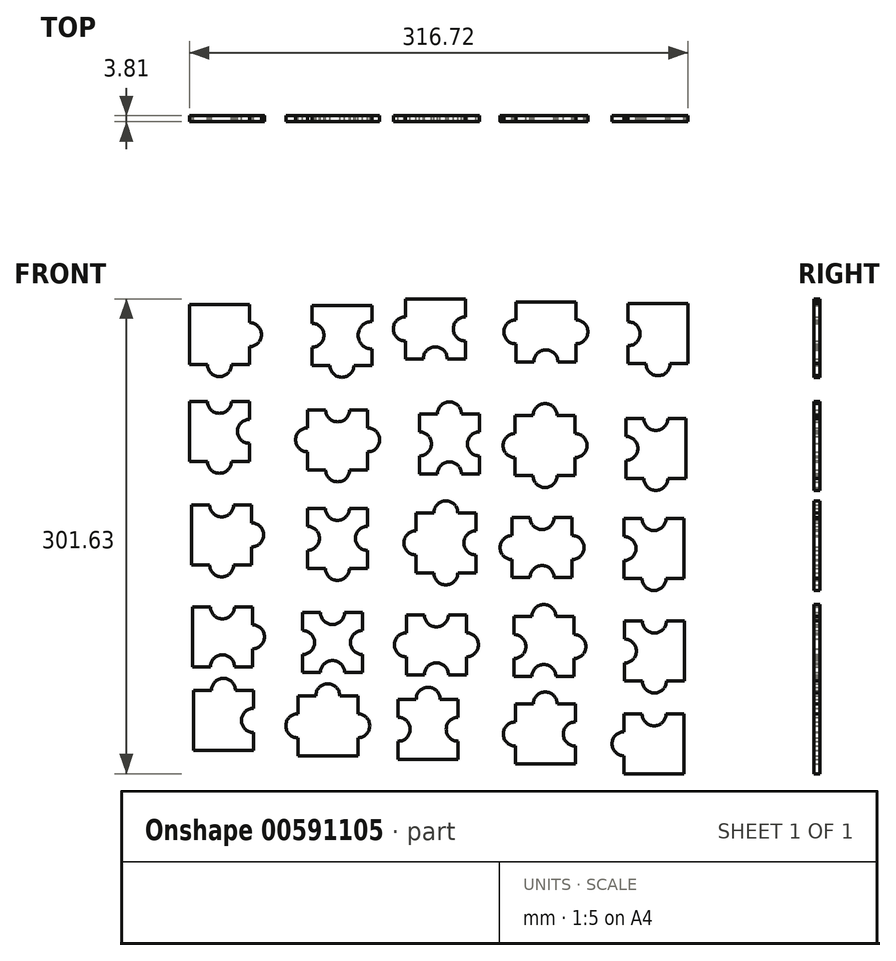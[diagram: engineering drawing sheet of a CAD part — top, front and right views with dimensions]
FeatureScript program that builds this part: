
annotation { "Feature Type Name" : "Feature", "Feature Type Description" : "" }
export const myFeature = defineFeature(function(context is Context, id is Id, definition is map)
    precondition{}
    {
        {
            var Q0;
            Q0=qCreatedBy(makeId("Front.planeOp"),FACE);
            var sketch = newSketch(context, id + "F0", { "sketchPlane" : qUnion([Q0])});
            skLineSegment(sketch, "E0", {"start": v(-60.62, 34.47) * mm, "end": v(-60.62, -3.63) * mm});
            skLineSegment(sketch, "E1", {"start": v(-60.62, 34.47) * mm, "end": v(-22.52, 34.47) * mm});
            skLineSegment(sketch, "E2", {"start": v(-22.52, 34.47) * mm, "end": v(-22.52, -3.63) * mm});
            skLineSegment(sketch, "E3", {"start": v(-22.52, -3.63) * mm, "end": v(-60.62, -3.63) * mm});
            skArc(sketch, "E4", {"start": v(-22.52, 23.04) * mm, "mid": v(-14.9, 15.42) * mm, "end": v(-22.52, 7.8) * mm});
            skArc(sketch, "E5", {"start": v(-33.95, -3.63) * mm, "mid": v(-41.57, -11.25) * mm, "end": v(-49.19, -3.63) * mm});
            skSolve(sketch);
        }
        {
            var Q0;
            Q0 = qSketchRegion(id + "F0", true);
            extrude(context, id + "F1", {"entities" : qUnion([Q0]), "depth" : 3.8 * mm, "offsetDistance" : 25.4 * mm});
        }
        {
            var Q0;
            Q0=qCreatedBy(makeId("Front.planeOp"),FACE);
            var sketch = newSketch(context, id + "F2", { "sketchPlane" : qUnion([Q0])});
            skLineSegment(sketch, "E6", {"start": v(-60.56, -26.98) * mm, "end": v(-60.56, -65.08) * mm});
            skLineSegment(sketch, "E7", {"start": v(-60.56, -26.98) * mm, "end": v(-49.13, -26.98) * mm});
            skLineSegment(sketch, "E8", {"start": v(-22.46, -26.98) * mm, "end": v(-22.46, -38.4) * mm});
            skLineSegment(sketch, "E9", {"start": v(-22.46, -65.08) * mm, "end": v(-33.89, -65.08) * mm});
            skArc(sketch, "E10", {"start": v(-33.89, -26.98) * mm, "mid": v(-41.5, -34.6) * mm, "end": v(-49.13, -26.98) * mm});
            skLineSegment(sketch, "E11.trimOffspring", {"start": v(-33.89, -26.98) * mm, "end": v(-22.46, -26.98) * mm});
            skArc(sketch, "E12", {"start": v(-22.46, -38.4) * mm, "mid": v(-30.08, -46.03) * mm, "end": v(-22.46, -53.65) * mm});
            skLineSegment(sketch, "E13.trimOffspring", {"start": v(-22.46, -53.65) * mm, "end": v(-22.46, -65.08) * mm});
            skArc(sketch, "E14", {"start": v(-33.89, -65.08) * mm, "mid": v(-41.5, -72.7) * mm, "end": v(-49.13, -65.08) * mm});
            skLineSegment(sketch, "E15.trimOffspring", {"start": v(-49.13, -65.08) * mm, "end": v(-60.56, -65.08) * mm});
            skSolve(sketch);
        }
        {
            var Q0;
            Q0 = qSketchRegion(id + "F2", true);
            extrude(context, id + "F3", {"entities" : qUnion([Q0]), "depth" : 3.8 * mm, "offsetDistance" : 25.4 * mm});
        }
        {
            var Q0;
            Q0=qCreatedBy(makeId("Front.planeOp"),FACE);
            var sketch = newSketch(context, id + "F4", { "sketchPlane" : qUnion([Q0])});
            skLineSegment(sketch, "E16", {"start": v(17.21, 34.03) * mm, "end": v(55.31, 34.03) * mm});
            skLineSegment(sketch, "E17", {"start": v(55.31, 34.03) * mm, "end": v(55.31, 23.73) * mm});
            skLineSegment(sketch, "E18", {"start": v(55.31, -4.07) * mm, "end": v(43.88, -4.07) * mm});
            skLineSegment(sketch, "E19", {"start": v(17.21, -4.07) * mm, "end": v(17.21, 7.36) * mm});
            skArc(sketch, "E20", {"start": v(17.21, 22.6) * mm, "mid": v(24.83, 14.98) * mm, "end": v(17.21, 7.36) * mm});
            skArc(sketch, "E21", {"start": v(43.88, -4.07) * mm, "mid": v(36.26, -11.7) * mm, "end": v(28.64, -4.07) * mm});
            skArc(sketch, "E22", {"start": v(55.31, 23.73) * mm, "mid": v(46.56, 14.98) * mm, "end": v(55.31, 6.23) * mm});
            skLineSegment(sketch, "E23.trimOffspring", {"start": v(55.31, 6.23) * mm, "end": v(55.31, -4.07) * mm});
            skLineSegment(sketch, "E24.trimOffspring", {"start": v(17.21, 22.6) * mm, "end": v(17.21, 34.03) * mm});
            skLineSegment(sketch, "E25.trimOffspring", {"start": v(28.64, -4.07) * mm, "end": v(17.21, -4.07) * mm});
            skSolve(sketch);
        }
        {
            var Q0;
            Q0=makeQuery(id+"F4.imprint","IMPRINT",FACE,{"disambiguationData":[TD([[makeQuery(id+"F4.imprint","IMPRINT",EDGE,{"derivedFrom":sQuery(id+"F4.wireOp",EDGE,"E16")}),-1.0]])]});
            extrude(context, id + "F5", {"entities" : qUnion([Q0]), "depth" : 3.8 * mm, "offsetDistance" : 25.4 * mm});
        }
        {
            var Q0;
            Q0=qCreatedBy(makeId("Front.planeOp"),FACE);
            var sketch = newSketch(context, id + "F6", { "sketchPlane" : qUnion([Q0])});
            skLineSegment(sketch, "E26", {"start": v(14.5, -32.37) * mm, "end": v(25.93, -32.37) * mm});
            skLineSegment(sketch, "E27", {"start": v(52.6, -32.37) * mm, "end": v(52.6, -43.8) * mm});
            skLineSegment(sketch, "E28", {"start": v(52.6, -70.47) * mm, "end": v(41.17, -70.47) * mm});
            skLineSegment(sketch, "E29", {"start": v(14.5, -70.47) * mm, "end": v(14.5, -59.04) * mm});
            skArc(sketch, "E30", {"start": v(41.17, -32.37) * mm, "mid": v(33.55, -40) * mm, "end": v(25.93, -32.37) * mm});
            skArc(sketch, "E31", {"start": v(14.5, -43.8) * mm, "mid": v(6.88, -51.42) * mm, "end": v(14.5, -59.04) * mm});
            skArc(sketch, "E32", {"start": v(52.6, -43.8) * mm, "mid": v(60.22, -51.42) * mm, "end": v(52.6, -59.04) * mm});
            skArc(sketch, "E33", {"start": v(41.17, -70.47) * mm, "mid": v(33.55, -78.1) * mm, "end": v(25.93, -70.47) * mm});
            skLineSegment(sketch, "E34.trimOffspring", {"start": v(41.17, -32.37) * mm, "end": v(52.6, -32.37) * mm});
            skLineSegment(sketch, "E35.trimOffspring", {"start": v(14.5, -43.8) * mm, "end": v(14.5, -32.37) * mm});
            skLineSegment(sketch, "E36.trimOffspring", {"start": v(52.6, -59.04) * mm, "end": v(52.6, -70.47) * mm});
            skLineSegment(sketch, "E37.trimOffspring", {"start": v(25.93, -70.47) * mm, "end": v(14.5, -70.47) * mm});
            skSolve(sketch);
        }
        {
            var Q0;
            Q0=makeQuery(id+"F6.imprint","IMPRINT",FACE,{"disambiguationData":[TD([[makeQuery(id+"F6.imprint","IMPRINT",EDGE,{"derivedFrom":sQuery(id+"F6.wireOp",EDGE,"E26")}),-1.0]])]});
            extrude(context, id + "F7", {"entities" : qUnion([Q0]), "depth" : 3.8 * mm, "offsetDistance" : 25.4 * mm});
        }
        {
            var Q0;
            Q0=qCreatedBy(makeId("Front.planeOp"),FACE);
            var sketch = newSketch(context, id + "F8", { "sketchPlane" : qUnion([Q0])});
            skLineSegment(sketch, "E38", {"start": v(76.49, 38.1) * mm, "end": v(114.59, 38.1) * mm});
            skLineSegment(sketch, "E39", {"start": v(114.59, 38.1) * mm, "end": v(114.59, 26.67) * mm});
            skLineSegment(sketch, "E40", {"start": v(114.59, 0) * mm, "end": v(103.16, 0) * mm});
            skLineSegment(sketch, "E41", {"start": v(76.49, 0) * mm, "end": v(76.49, 11.43) * mm});
            skArc(sketch, "E42", {"start": v(76.49, 26.67) * mm, "mid": v(68.87, 19.05) * mm, "end": v(76.49, 11.43) * mm});
            skArc(sketch, "E43", {"start": v(114.59, 26.67) * mm, "mid": v(106.97, 19.05) * mm, "end": v(114.59, 11.43) * mm});
            skArc(sketch, "E44", {"start": v(103.16, 0) * mm, "mid": v(95.54, 7.62) * mm, "end": v(87.92, 0) * mm});
            skLineSegment(sketch, "E45.trimOffspring", {"start": v(76.49, 26.67) * mm, "end": v(76.49, 38.1) * mm});
            skLineSegment(sketch, "E46.trimOffspring", {"start": v(114.59, 11.43) * mm, "end": v(114.59, 0) * mm});
            skLineSegment(sketch, "E47.trimOffspring", {"start": v(87.92, 0) * mm, "end": v(76.49, 0) * mm});
            skSolve(sketch);
        }
        {
            var Q0;
            Q0=makeQuery(id+"F8.imprint","IMPRINT",FACE,{"disambiguationData":[TD([[makeQuery(id+"F8.imprint","IMPRINT",EDGE,{"derivedFrom":sQuery(id+"F8.wireOp",EDGE,"E38")}),-1.0]])]});
            extrude(context, id + "F9", {"entities" : qUnion([Q0]), "depth" : 3.8 * mm, "offsetDistance" : 25.4 * mm});
        }
        {
            var Q0;
            Q0=qCreatedBy(makeId("Front.planeOp"),FACE);
            var sketch = newSketch(context, id + "F10", { "sketchPlane" : qUnion([Q0])});
            skLineSegment(sketch, "E48", {"start": v(123.53, -34.98) * mm, "end": v(123.53, -46.41) * mm});
            skLineSegment(sketch, "E49", {"start": v(123.53, -73.08) * mm, "end": v(112.1, -73.08) * mm});
            skLineSegment(sketch, "E50", {"start": v(85.43, -73.08) * mm, "end": v(85.43, -61.65) * mm});
            skArc(sketch, "E51", {"start": v(112.1, -34.98) * mm, "mid": v(104.48, -27.36) * mm, "end": v(96.86, -34.98) * mm});
            skArc(sketch, "E52", {"start": v(85.43, -46.41) * mm, "mid": v(93.05, -54.03) * mm, "end": v(85.43, -61.65) * mm});
            skArc(sketch, "E53", {"start": v(112.1, -73.08) * mm, "mid": v(104.48, -65.46) * mm, "end": v(96.86, -73.08) * mm});
            skArc(sketch, "E54", {"start": v(123.53, -46.41) * mm, "mid": v(115.91, -54.03) * mm, "end": v(123.53, -61.65) * mm});
            skLineSegment(sketch, "E55.trimOffspring", {"start": v(112.1, -34.98) * mm, "end": v(123.53, -34.98) * mm});
            skLineSegment(sketch, "E56.trimOffspring", {"start": v(123.53, -61.65) * mm, "end": v(123.53, -73.08) * mm});
            skLineSegment(sketch, "E57.trimOffspring", {"start": v(96.86, -73.08) * mm, "end": v(85.43, -73.08) * mm});
            skLineSegment(sketch, "E58.trimOffspring", {"start": v(85.43, -46.41) * mm, "end": v(85.43, -34.98) * mm});
            skLineSegment(sketch, "E59", {"start": v(85.43, -34.98) * mm, "end": v(96.86, -34.98) * mm});
            skSolve(sketch);
        }
        {
            var Q0;
            Q0=makeQuery(id+"F10.imprint","IMPRINT",FACE,{"disambiguationData":[TD([[makeQuery(id+"F10.imprint","IMPRINT",EDGE,{"derivedFrom":sQuery(id+"F10.wireOp",EDGE,"E48")}),-1.0]])]});
            extrude(context, id + "F11", {"entities" : qUnion([Q0]), "depth" : 3.8 * mm, "offsetDistance" : 25.4 * mm});
        }
        {
            var Q0;
            Q0=qCreatedBy(makeId("Front.planeOp"),FACE);
            var sketch = newSketch(context, id + "F12", { "sketchPlane" : qUnion([Q0])});
            skLineSegment(sketch, "E60", {"start": v(146.21, -36.05) * mm, "end": v(157.64, -36.05) * mm});
            skLineSegment(sketch, "E61", {"start": v(184.31, -74.15) * mm, "end": v(184.31, -62.72) * mm});
            skLineSegment(sketch, "E62", {"start": v(146.21, -36.05) * mm, "end": v(146.21, -47.48) * mm});
            skLineSegment(sketch, "E63", {"start": v(146.21, -74.15) * mm, "end": v(157.64, -74.15) * mm});
            skArc(sketch, "E64", {"start": v(172.88, -36.05) * mm, "mid": v(165.26, -28.43) * mm, "end": v(157.64, -36.05) * mm});
            skArc(sketch, "E65", {"start": v(146.21, -47.48) * mm, "mid": v(138.6, -55.1) * mm, "end": v(146.21, -62.72) * mm});
            skArc(sketch, "E66", {"start": v(172.88, -74.15) * mm, "mid": v(165.26, -81.77) * mm, "end": v(157.64, -74.15) * mm});
            skArc(sketch, "E67", {"start": v(184.31, -47.48) * mm, "mid": v(191.93, -55.1) * mm, "end": v(184.31, -62.72) * mm});
            skLineSegment(sketch, "E68.trimOffspring", {"start": v(172.88, -36.05) * mm, "end": v(184.31, -36.05) * mm});
            skLineSegment(sketch, "E69.trimOffspring", {"start": v(146.21, -62.72) * mm, "end": v(146.21, -74.15) * mm});
            skLineSegment(sketch, "E70.trimOffspring", {"start": v(172.88, -74.15) * mm, "end": v(184.31, -74.15) * mm});
            skLineSegment(sketch, "E71.trimOffspring", {"start": v(184.31, -47.48) * mm, "end": v(184.31, -36.05) * mm});
            skSolve(sketch);
        }
        {
            var Q0;
            Q0=makeQuery(id+"F12.imprint","IMPRINT",FACE,{"disambiguationData":[TD([[makeQuery(id+"F12.imprint","IMPRINT",EDGE,{"derivedFrom":sQuery(id+"F12.wireOp",EDGE,"E60")}),-1.0]])]});
            extrude(context, id + "F13", {"entities" : qUnion([Q0]), "depth" : 3.8 * mm, "offsetDistance" : 25.4 * mm});
        }
        {
            var Q0;
            Q0=qCreatedBy(makeId("Front.planeOp"),FACE);
            var sketch = newSketch(context, id + "F14", { "sketchPlane" : qUnion([Q0])});
            skLineSegment(sketch, "E72", {"start": v(146.72, 36.22) * mm, "end": v(184.82, 36.22) * mm});
            skLineSegment(sketch, "E73", {"start": v(184.82, 36.22) * mm, "end": v(184.82, 24.79) * mm});
            skLineSegment(sketch, "E74", {"start": v(184.82, -1.88) * mm, "end": v(173.39, -1.88) * mm});
            skLineSegment(sketch, "E75", {"start": v(146.72, -1.88) * mm, "end": v(146.72, 9.55) * mm});
            skArc(sketch, "E76", {"start": v(146.72, 24.79) * mm, "mid": v(139.1, 17.17) * mm, "end": v(146.72, 9.55) * mm});
            skArc(sketch, "E77", {"start": v(173.39, -1.88) * mm, "mid": v(165.77, 5.74) * mm, "end": v(158.15, -1.88) * mm});
            skArc(sketch, "E78", {"start": v(184.82, 9.55) * mm, "mid": v(192.44, 17.17) * mm, "end": v(184.82, 24.79) * mm});
            skLineSegment(sketch, "E79.trimOffspring", {"start": v(158.15, -1.88) * mm, "end": v(146.72, -1.88) * mm});
            skLineSegment(sketch, "E80.trimOffspring", {"start": v(184.82, 9.55) * mm, "end": v(184.82, -1.88) * mm});
            skLineSegment(sketch, "E81.trimOffspring", {"start": v(146.72, 24.79) * mm, "end": v(146.72, 36.22) * mm});
            skSolve(sketch);
        }
        {
            var Q0;
            Q0=makeQuery(id+"F14.imprint","IMPRINT",FACE,{"disambiguationData":[TD([[makeQuery(id+"F14.imprint","IMPRINT",EDGE,{"derivedFrom":sQuery(id+"F14.wireOp",EDGE,"E72")}),-1.0]])]});
            extrude(context, id + "F15", {"entities" : qUnion([Q0]), "depth" : 3.8 * mm, "offsetDistance" : 25.4 * mm});
        }
        {
            var Q0;
            Q0=qCreatedBy(makeId("Front.planeOp"),FACE);
            var sketch = newSketch(context, id + "F16", { "sketchPlane" : qUnion([Q0])});
            skLineSegment(sketch, "E82", {"start": v(218, 35) * mm, "end": v(256.1, 35) * mm});
            skLineSegment(sketch, "E83", {"start": v(256.1, 35) * mm, "end": v(256.1, -3.1) * mm});
            skLineSegment(sketch, "E84", {"start": v(256.1, -3.1) * mm, "end": v(244.67, -3.1) * mm});
            skLineSegment(sketch, "E85", {"start": v(218, -3.1) * mm, "end": v(218, 8.32) * mm});
            skArc(sketch, "E86", {"start": v(218, 8.32) * mm, "mid": v(225.62, 15.94) * mm, "end": v(218, 23.56) * mm});
            skArc(sketch, "E87", {"start": v(244.67, -3.1) * mm, "mid": v(237.05, -10.73) * mm, "end": v(229.43, -3.1) * mm});
            skLineSegment(sketch, "E88.trimOffspring", {"start": v(218, 23.56) * mm, "end": v(218, 35) * mm});
            skLineSegment(sketch, "E89.trimOffspring", {"start": v(229.43, -3.1) * mm, "end": v(218, -3.1) * mm});
            skSolve(sketch);
        }
        {
            var Q0;
            Q0=makeQuery(id+"F16.imprint","IMPRINT",FACE,{"disambiguationData":[TD([[makeQuery(id+"F16.imprint","IMPRINT",EDGE,{"derivedFrom":sQuery(id+"F16.wireOp",EDGE,"E82")}),-1.0]])]});
            extrude(context, id + "F17", {"entities" : qUnion([Q0]), "depth" : 3.8 * mm, "offsetDistance" : 25.4 * mm});
        }
        {
            var Q0;
            Q0=qCreatedBy(makeId("Front.planeOp"),FACE);
            var sketch = newSketch(context, id + "F18", { "sketchPlane" : qUnion([Q0])});
            skLineSegment(sketch, "E90", {"start": v(216.58, -37.87) * mm, "end": v(228, -37.87) * mm});
            skLineSegment(sketch, "E91", {"start": v(254.68, -37.87) * mm, "end": v(254.68, -75.97) * mm});
            skLineSegment(sketch, "E92", {"start": v(254.68, -75.97) * mm, "end": v(243.25, -75.97) * mm});
            skLineSegment(sketch, "E93", {"start": v(216.58, -75.97) * mm, "end": v(216.58, -64.54) * mm});
            skArc(sketch, "E94", {"start": v(243.25, -37.87) * mm, "mid": v(235.63, -45.49) * mm, "end": v(228, -37.87) * mm});
            skArc(sketch, "E95", {"start": v(216.58, -64.54) * mm, "mid": v(224.2, -56.92) * mm, "end": v(216.58, -49.3) * mm});
            skArc(sketch, "E96", {"start": v(243.25, -75.97) * mm, "mid": v(235.63, -83.59) * mm, "end": v(228, -75.97) * mm});
            skLineSegment(sketch, "E97.trimOffspring", {"start": v(243.25, -37.87) * mm, "end": v(254.68, -37.87) * mm});
            skLineSegment(sketch, "E98.trimOffspring", {"start": v(216.58, -49.3) * mm, "end": v(216.58, -37.87) * mm});
            skLineSegment(sketch, "E99.trimOffspring", {"start": v(228, -75.97) * mm, "end": v(216.58, -75.97) * mm});
            skSolve(sketch);
        }
        {
            var Q0;
            Q0=makeQuery(id+"F18.imprint","IMPRINT",FACE,{"disambiguationData":[TD([[makeQuery(id+"F18.imprint","IMPRINT",EDGE,{"derivedFrom":sQuery(id+"F18.wireOp",EDGE,"E90")}),-1.0]])]});
            extrude(context, id + "F19", {"entities" : qUnion([Q0]), "depth" : 3.8 * mm, "offsetDistance" : 25.4 * mm});
        }
        {
            var Q0;
            Q0=qCreatedBy(makeId("Front.planeOp"),FACE);
            var sketch = newSketch(context, id + "F20", { "sketchPlane" : qUnion([Q0])});
            skLineSegment(sketch, "E100", {"start": v(-59.22, -92.7) * mm, "end": v(-47.79, -92.7) * mm});
            skLineSegment(sketch, "E101", {"start": v(-21.12, -92.7) * mm, "end": v(-21.12, -104.14) * mm});
            skLineSegment(sketch, "E102", {"start": v(-21.12, -130.8) * mm, "end": v(-32.55, -130.8) * mm});
            skLineSegment(sketch, "E103", {"start": v(-59.22, -130.8) * mm, "end": v(-59.22, -92.7) * mm});
            skArc(sketch, "E104", {"start": v(-32.55, -92.7) * mm, "mid": v(-40.17, -100.33) * mm, "end": v(-47.79, -92.7) * mm});
            skArc(sketch, "E105", {"start": v(-21.12, -104.14) * mm, "mid": v(-13.5, -111.76) * mm, "end": v(-21.12, -119.38) * mm});
            skArc(sketch, "E106", {"start": v(-32.55, -130.8) * mm, "mid": v(-40.17, -138.43) * mm, "end": v(-47.79, -130.8) * mm});
            skLineSegment(sketch, "E107.trimOffspring", {"start": v(-32.55, -92.7) * mm, "end": v(-21.12, -92.7) * mm});
            skLineSegment(sketch, "E108.trimOffspring", {"start": v(-21.12, -119.38) * mm, "end": v(-21.12, -130.8) * mm});
            skLineSegment(sketch, "E109.trimOffspring", {"start": v(-47.79, -130.8) * mm, "end": v(-59.22, -130.8) * mm});
            skSolve(sketch);
        }
        {
            var Q0;
            Q0=makeQuery(id+"F20.imprint","IMPRINT",FACE,{"disambiguationData":[TD([[makeQuery(id+"F20.imprint","IMPRINT",EDGE,{"derivedFrom":sQuery(id+"F20.wireOp",EDGE,"E100")}),-1.0]])]});
            extrude(context, id + "F21", {"entities" : qUnion([Q0]), "depth" : 3.8 * mm, "offsetDistance" : 25.4 * mm});
        }
        {
            var Q0;
            Q0=qCreatedBy(makeId("Front.planeOp"),FACE);
            var sketch = newSketch(context, id + "F22", { "sketchPlane" : qUnion([Q0])});
            skLineSegment(sketch, "E110", {"start": v(14.35, -94.97) * mm, "end": v(25.78, -94.97) * mm});
            skLineSegment(sketch, "E111", {"start": v(52.45, -94.97) * mm, "end": v(52.45, -106.4) * mm});
            skLineSegment(sketch, "E112", {"start": v(52.45, -133.07) * mm, "end": v(41.02, -133.07) * mm});
            skLineSegment(sketch, "E113", {"start": v(14.35, -133.07) * mm, "end": v(14.35, -121.64) * mm});
            skArc(sketch, "E114", {"start": v(41.02, -94.97) * mm, "mid": v(33.4, -102.6) * mm, "end": v(25.78, -94.97) * mm});
            skArc(sketch, "E115", {"start": v(14.35, -121.64) * mm, "mid": v(21.97, -114.02) * mm, "end": v(14.35, -106.4) * mm});
            skArc(sketch, "E116", {"start": v(41.02, -133.07) * mm, "mid": v(33.4, -140.7) * mm, "end": v(25.78, -133.07) * mm});
            skArc(sketch, "E117", {"start": v(52.45, -106.4) * mm, "mid": v(44.83, -114.02) * mm, "end": v(52.45, -121.64) * mm});
            skLineSegment(sketch, "E118.trimOffspring", {"start": v(41.02, -94.97) * mm, "end": v(52.45, -94.97) * mm});
            skLineSegment(sketch, "E119.trimOffspring", {"start": v(52.45, -121.64) * mm, "end": v(52.45, -133.07) * mm});
            skLineSegment(sketch, "E120.trimOffspring", {"start": v(25.78, -133.07) * mm, "end": v(14.35, -133.07) * mm});
            skLineSegment(sketch, "E121.trimOffspring", {"start": v(14.35, -106.4) * mm, "end": v(14.35, -94.97) * mm});
            skSolve(sketch);
        }
        {
            var Q0;
            Q0=makeQuery(id+"F22.imprint","IMPRINT",FACE,{"disambiguationData":[TD([[makeQuery(id+"F22.imprint","IMPRINT",EDGE,{"derivedFrom":sQuery(id+"F22.wireOp",EDGE,"E110")}),-1.0]])]});
            extrude(context, id + "F23", {"entities" : qUnion([Q0]), "depth" : 3.8 * mm, "offsetDistance" : 25.4 * mm});
        }
        {
            var Q0;
            Q0=qCreatedBy(makeId("Front.planeOp"),FACE);
            var sketch = newSketch(context, id + "F24", { "sketchPlane" : qUnion([Q0])});
            skLineSegment(sketch, "E122", {"start": v(83.18, -97.86) * mm, "end": v(94.61, -97.86) * mm});
            skLineSegment(sketch, "E123", {"start": v(121.28, -97.86) * mm, "end": v(121.28, -109.29) * mm});
            skLineSegment(sketch, "E124", {"start": v(121.28, -135.96) * mm, "end": v(109.85, -135.96) * mm});
            skLineSegment(sketch, "E125", {"start": v(83.18, -135.96) * mm, "end": v(83.18, -124.53) * mm});
            skArc(sketch, "E126", {"start": v(109.85, -97.86) * mm, "mid": v(102.23, -90.24) * mm, "end": v(94.61, -97.86) * mm});
            skArc(sketch, "E127", {"start": v(83.18, -109.29) * mm, "mid": v(75.56, -116.9) * mm, "end": v(83.18, -124.53) * mm});
            skArc(sketch, "E128", {"start": v(109.85, -135.96) * mm, "mid": v(102.23, -143.58) * mm, "end": v(94.61, -135.96) * mm});
            skArc(sketch, "E129", {"start": v(121.28, -109.29) * mm, "mid": v(113.66, -116.9) * mm, "end": v(121.28, -124.53) * mm});
            skLineSegment(sketch, "E130.trimOffspring", {"start": v(121.28, -124.53) * mm, "end": v(121.28, -135.96) * mm});
            skLineSegment(sketch, "E131.trimOffspring", {"start": v(109.85, -97.86) * mm, "end": v(121.28, -97.86) * mm});
            skLineSegment(sketch, "E132.trimOffspring", {"start": v(83.18, -109.29) * mm, "end": v(83.18, -97.86) * mm});
            skLineSegment(sketch, "E133.trimOffspring", {"start": v(94.61, -135.96) * mm, "end": v(83.18, -135.96) * mm});
            skSolve(sketch);
        }
        {
            var Q0;
            Q0=makeQuery(id+"F24.imprint","IMPRINT",FACE,{"disambiguationData":[TD([[makeQuery(id+"F24.imprint","IMPRINT",EDGE,{"derivedFrom":sQuery(id+"F24.wireOp",EDGE,"E122")}),-1.0]])]});
            extrude(context, id + "F25", {"entities" : qUnion([Q0]), "depth" : 3.8 * mm, "offsetDistance" : 25.4 * mm});
        }
        {
            var Q0;
            Q0=qCreatedBy(makeId("Front.planeOp"),FACE);
            var sketch = newSketch(context, id + "F26", { "sketchPlane" : qUnion([Q0])});
            skLineSegment(sketch, "E134", {"start": v(182.47, -100.82) * mm, "end": v(182.47, -112.25) * mm});
            skLineSegment(sketch, "E135", {"start": v(182.47, -138.92) * mm, "end": v(171.04, -138.92) * mm});
            skLineSegment(sketch, "E136", {"start": v(144.37, -138.92) * mm, "end": v(144.37, -127.5) * mm});
            skArc(sketch, "E137", {"start": v(171.04, -100.82) * mm, "mid": v(163.42, -108.44) * mm, "end": v(155.8, -100.82) * mm});
            skArc(sketch, "E138", {"start": v(144.37, -112.25) * mm, "mid": v(136.75, -119.87) * mm, "end": v(144.37, -127.5) * mm});
            skArc(sketch, "E139", {"start": v(171.04, -138.92) * mm, "mid": v(163.42, -131.3) * mm, "end": v(155.8, -138.92) * mm});
            skArc(sketch, "E140", {"start": v(182.47, -127.5) * mm, "mid": v(190.09, -119.87) * mm, "end": v(182.47, -112.25) * mm});
            skPoint(sketch, "E140.startSnap0", {"position": v(182.47, -119.87) * mm});
            skLineSegment(sketch, "E141.trimOffspring", {"start": v(171.04, -100.82) * mm, "end": v(182.47, -100.82) * mm});
            skLineSegment(sketch, "E142.trimOffspring", {"start": v(182.47, -127.5) * mm, "end": v(182.47, -138.92) * mm});
            skLineSegment(sketch, "E143.trimOffspring", {"start": v(155.8, -138.92) * mm, "end": v(144.37, -138.92) * mm});
            skLineSegment(sketch, "E144.trimOffspring", {"start": v(144.37, -112.25) * mm, "end": v(144.37, -100.82) * mm});
            skLineSegment(sketch, "E145", {"start": v(144.37, -100.82) * mm, "end": v(155.8, -100.82) * mm});
            skSolve(sketch);
        }
        {
            var Q0;
            Q0=makeQuery(id+"F26.imprint","IMPRINT",FACE,{"disambiguationData":[TD([[makeQuery(id+"F26.imprint","IMPRINT",EDGE,{"derivedFrom":sQuery(id+"F26.wireOp",EDGE,"E134")}),-1.0]])]});
            extrude(context, id + "F27", {"entities" : qUnion([Q0]), "depth" : 3.8 * mm, "offsetDistance" : 25.4 * mm});
        }
        {
            var Q0;
            Q0=qCreatedBy(makeId("Front.planeOp"),FACE);
            var sketch = newSketch(context, id + "F28", { "sketchPlane" : qUnion([Q0])});
            skLineSegment(sketch, "E146", {"start": v(215.4, -101.4) * mm, "end": v(226.83, -101.4) * mm});
            skLineSegment(sketch, "E147", {"start": v(253.5, -101.4) * mm, "end": v(253.5, -139.5) * mm});
            skLineSegment(sketch, "E148", {"start": v(253.5, -139.5) * mm, "end": v(242.07, -139.5) * mm});
            skLineSegment(sketch, "E149", {"start": v(215.4, -139.5) * mm, "end": v(215.4, -128.07) * mm});
            skArc(sketch, "E150", {"start": v(242.07, -101.4) * mm, "mid": v(234.45, -109.02) * mm, "end": v(226.83, -101.4) * mm});
            skArc(sketch, "E151", {"start": v(215.4, -112.83) * mm, "mid": v(223.02, -120.45) * mm, "end": v(215.4, -128.07) * mm});
            skArc(sketch, "E152", {"start": v(242.07, -139.5) * mm, "mid": v(234.45, -147.12) * mm, "end": v(226.83, -139.5) * mm});
            skLineSegment(sketch, "E153.trimOffspring", {"start": v(215.4, -112.83) * mm, "end": v(215.4, -101.4) * mm});
            skLineSegment(sketch, "E154.trimOffspring", {"start": v(242.07, -101.4) * mm, "end": v(253.5, -101.4) * mm});
            skLineSegment(sketch, "E155.trimOffspring", {"start": v(226.83, -139.5) * mm, "end": v(215.4, -139.5) * mm});
            skSolve(sketch);
        }
        {
            var Q0;
            Q0=makeQuery(id+"F28.imprint","IMPRINT",FACE,{"disambiguationData":[TD([[makeQuery(id+"F28.imprint","IMPRINT",EDGE,{"derivedFrom":sQuery(id+"F28.wireOp",EDGE,"E146")}),-1.0]])]});
            extrude(context, id + "F29", {"entities" : qUnion([Q0]), "depth" : 3.8 * mm, "offsetDistance" : 25.4 * mm});
        }
        {
            var Q0;
            Q0=qCreatedBy(makeId("Front.planeOp"),FACE);
            var sketch = newSketch(context, id + "F30", { "sketchPlane" : qUnion([Q0])});
            skLineSegment(sketch, "E156", {"start": v(-58.69, -157.48) * mm, "end": v(-47.26, -157.48) * mm});
            skLineSegment(sketch, "E157", {"start": v(-20.59, -157.48) * mm, "end": v(-20.59, -168.91) * mm});
            skLineSegment(sketch, "E158", {"start": v(-20.59, -195.58) * mm, "end": v(-32.02, -195.58) * mm});
            skLineSegment(sketch, "E159", {"start": v(-58.69, -195.58) * mm, "end": v(-58.69, -157.48) * mm});
            skArc(sketch, "E160", {"start": v(-32.02, -157.48) * mm, "mid": v(-39.64, -165.1) * mm, "end": v(-47.26, -157.48) * mm});
            skArc(sketch, "E161", {"start": v(-32.02, -195.58) * mm, "mid": v(-39.64, -187.96) * mm, "end": v(-47.26, -195.58) * mm});
            skArc(sketch, "E162", {"start": v(-20.59, -168.91) * mm, "mid": v(-12.97, -176.53) * mm, "end": v(-20.59, -184.15) * mm});
            skLineSegment(sketch, "E163.trimOffspring", {"start": v(-32.02, -157.48) * mm, "end": v(-20.59, -157.48) * mm});
            skLineSegment(sketch, "E164.trimOffspring", {"start": v(-20.59, -184.15) * mm, "end": v(-20.59, -195.58) * mm});
            skLineSegment(sketch, "E165.trimOffspring", {"start": v(-47.26, -195.58) * mm, "end": v(-58.69, -195.58) * mm});
            skSolve(sketch);
        }
        {
            var Q0;
            Q0=makeQuery(id+"F30.imprint","IMPRINT",FACE,{"disambiguationData":[TD([[makeQuery(id+"F30.imprint","IMPRINT",EDGE,{"derivedFrom":sQuery(id+"F30.wireOp",EDGE,"E156")}),-1.0]])]});
            extrude(context, id + "F31", {"entities" : qUnion([Q0]), "depth" : 3.8 * mm, "offsetDistance" : 25.4 * mm});
        }
        {
            var Q0;
            Q0=qCreatedBy(makeId("Front.planeOp"),FACE);
            var sketch = newSketch(context, id + "F32", { "sketchPlane" : qUnion([Q0])});
            skLineSegment(sketch, "E166", {"start": v(11.24, -161.11) * mm, "end": v(22.67, -161.11) * mm});
            skLineSegment(sketch, "E167", {"start": v(49.34, -161.11) * mm, "end": v(49.34, -172.54) * mm});
            skLineSegment(sketch, "E168", {"start": v(49.34, -199.21) * mm, "end": v(37.9, -199.21) * mm});
            skLineSegment(sketch, "E169", {"start": v(11.24, -199.21) * mm, "end": v(11.24, -187.78) * mm});
            skArc(sketch, "E170", {"start": v(37.9, -161.11) * mm, "mid": v(30.29, -168.73) * mm, "end": v(22.67, -161.11) * mm});
            skPoint(sketch, "E171.startSnap0", {"position": v(30.29, -168.73) * mm});
            skArc(sketch, "E172", {"start": v(11.24, -172.54) * mm, "mid": v(18.86, -180.16) * mm, "end": v(11.24, -187.78) * mm});
            skArc(sketch, "E173", {"start": v(37.9, -199.21) * mm, "mid": v(30.29, -191.6) * mm, "end": v(22.67, -199.21) * mm});
            skArc(sketch, "E174", {"start": v(49.34, -172.54) * mm, "mid": v(41.72, -180.16) * mm, "end": v(49.34, -187.78) * mm});
            skLineSegment(sketch, "E175.trimOffspring", {"start": v(37.9, -161.11) * mm, "end": v(49.34, -161.11) * mm});
            skLineSegment(sketch, "E176.trimOffspring", {"start": v(11.24, -172.54) * mm, "end": v(11.24, -161.11) * mm});
            skLineSegment(sketch, "E177.trimOffspring", {"start": v(22.67, -199.21) * mm, "end": v(11.24, -199.21) * mm});
            skLineSegment(sketch, "E178.trimOffspring", {"start": v(49.34, -187.78) * mm, "end": v(49.34, -199.21) * mm});
            skSolve(sketch);
        }
        {
            var Q0;
            Q0=makeQuery(id+"F32.imprint","IMPRINT",FACE,{"disambiguationData":[TD([[makeQuery(id+"F32.imprint","IMPRINT",EDGE,{"derivedFrom":sQuery(id+"F32.wireOp",EDGE,"E166")}),-1.0]])]});
            extrude(context, id + "F33", {"entities" : qUnion([Q0]), "depth" : 3.8 * mm, "offsetDistance" : 25.4 * mm});
        }
        {
            var Q0;
            Q0=qCreatedBy(makeId("Front.planeOp"),FACE);
            var sketch = newSketch(context, id + "F34", { "sketchPlane" : qUnion([Q0])});
            skLineSegment(sketch, "E179", {"start": v(77.18, -162.59) * mm, "end": v(88.61, -162.59) * mm});
            skLineSegment(sketch, "E180", {"start": v(115.28, -162.59) * mm, "end": v(115.28, -174.02) * mm});
            skLineSegment(sketch, "E181", {"start": v(115.28, -200.69) * mm, "end": v(103.85, -200.69) * mm});
            skLineSegment(sketch, "E182", {"start": v(77.18, -200.69) * mm, "end": v(77.18, -189.26) * mm});
            skArc(sketch, "E183", {"start": v(103.85, -162.59) * mm, "mid": v(96.23, -170.2) * mm, "end": v(88.61, -162.59) * mm});
            skArc(sketch, "E184", {"start": v(77.18, -174.02) * mm, "mid": v(69.56, -181.64) * mm, "end": v(77.18, -189.26) * mm});
            skArc(sketch, "E185", {"start": v(103.85, -200.69) * mm, "mid": v(96.23, -193.07) * mm, "end": v(88.61, -200.69) * mm});
            skArc(sketch, "E186", {"start": v(115.28, -174.02) * mm, "mid": v(122.9, -181.64) * mm, "end": v(115.28, -189.26) * mm});
            skLineSegment(sketch, "E187.trimOffspring", {"start": v(103.85, -162.59) * mm, "end": v(115.28, -162.59) * mm});
            skLineSegment(sketch, "E188.trimOffspring", {"start": v(115.28, -189.26) * mm, "end": v(115.28, -200.69) * mm});
            skLineSegment(sketch, "E189.trimOffspring", {"start": v(88.61, -200.69) * mm, "end": v(77.18, -200.69) * mm});
            skLineSegment(sketch, "E190.trimOffspring", {"start": v(77.18, -174.02) * mm, "end": v(77.18, -162.59) * mm});
            skSolve(sketch);
        }
        {
            var Q0;
            Q0=makeQuery(id+"F34.imprint","IMPRINT",FACE,{"disambiguationData":[TD([[makeQuery(id+"F34.imprint","IMPRINT",EDGE,{"derivedFrom":sQuery(id+"F34.wireOp",EDGE,"E179")}),-1.0]])]});
            extrude(context, id + "F35", {"entities" : qUnion([Q0]), "depth" : 3.8 * mm, "offsetDistance" : 25.4 * mm});
        }
        {
            var Q0;
            Q0=qCreatedBy(makeId("Front.planeOp"),FACE);
            var sketch = newSketch(context, id + "F36", { "sketchPlane" : qUnion([Q0])});
            skLineSegment(sketch, "E191", {"start": v(145.5, -163.65) * mm, "end": v(156.93, -163.65) * mm});
            skLineSegment(sketch, "E192", {"start": v(183.6, -163.65) * mm, "end": v(183.6, -175.08) * mm});
            skLineSegment(sketch, "E193", {"start": v(183.6, -201.75) * mm, "end": v(172.17, -201.75) * mm});
            skLineSegment(sketch, "E194", {"start": v(145.5, -201.75) * mm, "end": v(145.5, -190.32) * mm});
            skArc(sketch, "E195", {"start": v(172.17, -163.65) * mm, "mid": v(164.55, -156.03) * mm, "end": v(156.93, -163.65) * mm});
            skArc(sketch, "E196", {"start": v(145.5, -175.08) * mm, "mid": v(153.12, -182.7) * mm, "end": v(145.5, -190.32) * mm});
            skArc(sketch, "E197", {"start": v(183.6, -190.32) * mm, "mid": v(191.22, -182.7) * mm, "end": v(183.6, -175.08) * mm});
            skArc(sketch, "E198", {"start": v(172.17, -201.75) * mm, "mid": v(164.55, -194.13) * mm, "end": v(156.93, -201.75) * mm});
            skLineSegment(sketch, "E199.trimOffspring", {"start": v(172.17, -163.65) * mm, "end": v(183.6, -163.65) * mm});
            skLineSegment(sketch, "E200.trimOffspring", {"start": v(183.6, -190.32) * mm, "end": v(183.6, -201.75) * mm});
            skLineSegment(sketch, "E201.trimOffspring", {"start": v(156.93, -201.75) * mm, "end": v(145.5, -201.75) * mm});
            skLineSegment(sketch, "E202.trimOffspring", {"start": v(145.5, -175.08) * mm, "end": v(145.5, -163.65) * mm});
            skSolve(sketch);
        }
        {
            var Q0;
            Q0 = qSketchRegion(id + "F36", true);
            extrude(context, id + "F37", {"entities" : qUnion([Q0]), "depth" : 3.8 * mm, "offsetDistance" : 25.4 * mm});
        }
        {
            var Q0;
            Q0=qCreatedBy(makeId("Front.planeOp"),FACE);
            var sketch = newSketch(context, id + "F38", { "sketchPlane" : qUnion([Q0])});
            skLineSegment(sketch, "E203", {"start": v(215.68, -166.55) * mm, "end": v(227.11, -166.55) * mm});
            skLineSegment(sketch, "E204", {"start": v(253.78, -166.55) * mm, "end": v(253.78, -204.65) * mm});
            skLineSegment(sketch, "E205", {"start": v(253.78, -204.65) * mm, "end": v(242.35, -204.65) * mm});
            skLineSegment(sketch, "E206", {"start": v(215.68, -204.65) * mm, "end": v(215.68, -193.22) * mm});
            skArc(sketch, "E207", {"start": v(242.35, -166.55) * mm, "mid": v(234.73, -174.17) * mm, "end": v(227.11, -166.55) * mm});
            skArc(sketch, "E208", {"start": v(215.68, -177.98) * mm, "mid": v(223.3, -185.6) * mm, "end": v(215.68, -193.22) * mm});
            skArc(sketch, "E209", {"start": v(242.35, -204.65) * mm, "mid": v(234.73, -212.27) * mm, "end": v(227.11, -204.65) * mm});
            skLineSegment(sketch, "E210.trimOffspring", {"start": v(242.35, -166.55) * mm, "end": v(253.78, -166.55) * mm});
            skLineSegment(sketch, "E211.trimOffspring", {"start": v(215.68, -177.98) * mm, "end": v(215.68, -166.55) * mm});
            skLineSegment(sketch, "E212.trimOffspring", {"start": v(227.11, -204.65) * mm, "end": v(215.68, -204.65) * mm});
            skSolve(sketch);
        }
        {
            var Q0;
            Q0 = qSketchRegion(id + "F38", true);
            extrude(context, id + "F39", {"entities" : qUnion([Q0]), "depth" : 3.8 * mm, "offsetDistance" : 25.4 * mm});
        }
        {
            var Q0;
            Q0=qCreatedBy(makeId("Front.planeOp"),FACE);
            var sketch = newSketch(context, id + "F40", { "sketchPlane" : qUnion([Q0])});
            skLineSegment(sketch, "E213", {"start": v(-19.99, -210.62) * mm, "end": v(-19.99, -222.05) * mm});
            skLineSegment(sketch, "E214", {"start": v(-19.99, -248.72) * mm, "end": v(-58.09, -248.72) * mm});
            skLineSegment(sketch, "E215", {"start": v(-58.09, -248.72) * mm, "end": v(-58.09, -210.62) * mm});
            skArc(sketch, "E216", {"start": v(-31.42, -210.62) * mm, "mid": v(-39.04, -203) * mm, "end": v(-46.66, -210.62) * mm});
            skArc(sketch, "E217", {"start": v(-19.99, -222.05) * mm, "mid": v(-27.6, -229.67) * mm, "end": v(-19.99, -237.29) * mm});
            skLineSegment(sketch, "E218.trimOffspring", {"start": v(-31.42, -210.62) * mm, "end": v(-19.99, -210.62) * mm});
            skLineSegment(sketch, "E219.trimOffspring", {"start": v(-19.99, -237.29) * mm, "end": v(-19.99, -248.72) * mm});
            skLineSegment(sketch, "E220", {"start": v(-58.09, -210.62) * mm, "end": v(-46.66, -210.62) * mm});
            skSolve(sketch);
        }
        {
            var Q0;
            Q0 = qSketchRegion(id + "F40", true);
            extrude(context, id + "F41", {"entities" : qUnion([Q0]), "depth" : 3.8 * mm, "offsetDistance" : 25.4 * mm});
        }
        {
            var Q0;
            Q0=qCreatedBy(makeId("Front.planeOp"),FACE);
            var sketch = newSketch(context, id + "F42", { "sketchPlane" : qUnion([Q0])});
            skLineSegment(sketch, "E221", {"start": v(8.21, -214) * mm, "end": v(19.64, -214) * mm});
            skLineSegment(sketch, "E222", {"start": v(46.31, -252.1) * mm, "end": v(8.21, -252.1) * mm});
            skLineSegment(sketch, "E223", {"start": v(8.21, -252.1) * mm, "end": v(8.21, -240.66) * mm});
            skArc(sketch, "E224", {"start": v(8.21, -225.42) * mm, "mid": v(0.6, -233.04) * mm, "end": v(8.21, -240.66) * mm});
            skArc(sketch, "E225", {"start": v(34.88, -214) * mm, "mid": v(27.26, -206.37) * mm, "end": v(19.64, -214) * mm});
            skArc(sketch, "E226", {"start": v(46.31, -225.42) * mm, "mid": v(53.93, -233.04) * mm, "end": v(46.31, -240.66) * mm});
            skLineSegment(sketch, "E227.trimOffspring", {"start": v(34.88, -214) * mm, "end": v(46.31, -214) * mm});
            skLineSegment(sketch, "E228.trimOffspring", {"start": v(8.21, -225.42) * mm, "end": v(8.21, -214) * mm});
            skLineSegment(sketch, "E229.trimOffspring", {"start": v(46.31, -240.66) * mm, "end": v(46.31, -252.1) * mm});
            skLineSegment(sketch, "E230", {"start": v(46.31, -214) * mm, "end": v(46.31, -225.42) * mm});
            skSolve(sketch);
        }
        {
            var Q0;
            Q0 = qSketchRegion(id + "F42", true);
            extrude(context, id + "F43", {"entities" : qUnion([Q0]), "depth" : 3.8 * mm, "offsetDistance" : 25.4 * mm});
        }
        {
            var Q0;
            Q0=qCreatedBy(makeId("Front.planeOp"),FACE);
            var sketch = newSketch(context, id + "F44", { "sketchPlane" : qUnion([Q0])});
            skLineSegment(sketch, "E231", {"start": v(72, -216.2) * mm, "end": v(83.42, -216.2) * mm});
            skLineSegment(sketch, "E232", {"start": v(110.1, -254.3) * mm, "end": v(72, -254.3) * mm});
            skArc(sketch, "E233", {"start": v(98.66, -216.2) * mm, "mid": v(91.04, -208.57) * mm, "end": v(83.42, -216.2) * mm});
            skArc(sketch, "E234", {"start": v(72, -227.62) * mm, "mid": v(79.61, -235.24) * mm, "end": v(72, -242.86) * mm});
            skArc(sketch, "E235", {"start": v(110.1, -227.62) * mm, "mid": v(102.47, -235.24) * mm, "end": v(110.1, -242.86) * mm});
            skLineSegment(sketch, "E236.trimOffspring", {"start": v(110.1, -242.86) * mm, "end": v(110.1, -254.3) * mm});
            skLineSegment(sketch, "E237.trimOffspring", {"start": v(98.66, -216.2) * mm, "end": v(110.1, -216.2) * mm});
            skLineSegment(sketch, "E238.trimOffspring", {"start": v(72, -227.62) * mm, "end": v(72, -216.2) * mm});
            skLineSegment(sketch, "E239", {"start": v(72, -254.3) * mm, "end": v(72, -242.86) * mm});
            skLineSegment(sketch, "E240", {"start": v(110.1, -216.2) * mm, "end": v(110.1, -227.62) * mm});
            skSolve(sketch);
        }
        {
            var Q0;
            Q0 = qSketchRegion(id + "F44", true);
            extrude(context, id + "F45", {"entities" : qUnion([Q0]), "depth" : 3.8 * mm, "offsetDistance" : 25.4 * mm});
        }
        {
            var Q0;
            Q0=qCreatedBy(makeId("Front.planeOp"),FACE);
            var sketch = newSketch(context, id + "F46", { "sketchPlane" : qUnion([Q0])});
            skLineSegment(sketch, "E241", {"start": v(184.45, -219.22) * mm, "end": v(184.45, -230.65) * mm});
            skLineSegment(sketch, "E242", {"start": v(184.45, -257.32) * mm, "end": v(146.35, -257.32) * mm});
            skLineSegment(sketch, "E243", {"start": v(146.35, -257.32) * mm, "end": v(146.35, -245.89) * mm});
            skArc(sketch, "E244", {"start": v(173.02, -219.22) * mm, "mid": v(165.4, -211.6) * mm, "end": v(157.78, -219.22) * mm});
            skArc(sketch, "E245", {"start": v(146.35, -230.65) * mm, "mid": v(138.73, -238.27) * mm, "end": v(146.35, -245.89) * mm});
            skArc(sketch, "E246", {"start": v(184.45, -230.65) * mm, "mid": v(176.83, -238.27) * mm, "end": v(184.45, -245.89) * mm});
            skLineSegment(sketch, "E247.trimOffspring", {"start": v(184.45, -245.89) * mm, "end": v(184.45, -257.32) * mm});
            skLineSegment(sketch, "E248.trimOffspring", {"start": v(146.35, -230.65) * mm, "end": v(146.35, -219.22) * mm});
            skLineSegment(sketch, "E249.trimOffspring", {"start": v(173.02, -219.22) * mm, "end": v(184.45, -219.22) * mm});
            skLineSegment(sketch, "E250", {"start": v(146.35, -219.22) * mm, "end": v(157.78, -219.22) * mm});
            skSolve(sketch);
        }
        {
            var Q0;
            Q0 = qSketchRegion(id + "F46", true);
            extrude(context, id + "F47", {"entities" : qUnion([Q0]), "depth" : 3.8 * mm, "offsetDistance" : 25.4 * mm});
        }
        {
            var Q0;
            Q0=qCreatedBy(makeId("Front.planeOp"),FACE);
            var sketch = newSketch(context, id + "F48", { "sketchPlane" : qUnion([Q0])});
            skLineSegment(sketch, "E251", {"start": v(253.54, -225.43) * mm, "end": v(253.54, -263.53) * mm});
            skLineSegment(sketch, "E252", {"start": v(253.54, -263.53) * mm, "end": v(215.44, -263.53) * mm});
            skLineSegment(sketch, "E253", {"start": v(215.44, -263.53) * mm, "end": v(215.44, -252.1) * mm});
            skArc(sketch, "E254", {"start": v(242.11, -225.43) * mm, "mid": v(234.5, -233.05) * mm, "end": v(226.87, -225.43) * mm});
            skArc(sketch, "E255", {"start": v(215.44, -236.86) * mm, "mid": v(207.82, -244.48) * mm, "end": v(215.44, -252.1) * mm});
            skLineSegment(sketch, "E256.trimOffspring", {"start": v(242.11, -225.43) * mm, "end": v(253.54, -225.43) * mm});
            skLineSegment(sketch, "E257.trimOffspring", {"start": v(215.44, -236.86) * mm, "end": v(215.44, -225.43) * mm});
            skLineSegment(sketch, "E258", {"start": v(215.44, -225.43) * mm, "end": v(226.87, -225.43) * mm});
            skSolve(sketch);
        }
        {
            var Q0;
            Q0 = qSketchRegion(id + "F48", true);
            var Q1;
            Q1=makeQuery(id+"F48.imprint","IMPRINT",FACE,{"disambiguationData":[TD([[makeQuery(id+"F48.imprint","IMPRINT",EDGE,{"derivedFrom":sQuery(id+"F48.wireOp",EDGE,"E251")}),-1.0]])]});
            extrude(context, id + "F49", {"entities" : qUnion([Q0, Q1]), "depth" : 3.8 * mm, "offsetDistance" : 25.4 * mm});
        }
    });
